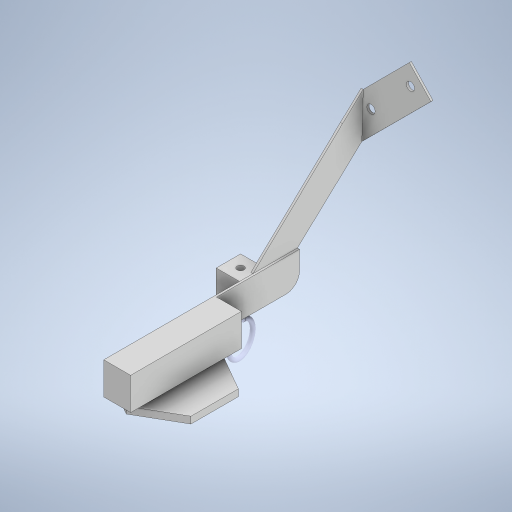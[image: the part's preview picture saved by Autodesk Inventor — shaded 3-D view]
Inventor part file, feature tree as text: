
AUTODESK INVENTOR PART (.ipt)
format: ipt  version: 2023 (Build 270158000, 158)  size: 340,992 bytes
history: native  units: in
note: dims shown in document units (in); Inventor stores cm internally (conversion verified against a paired STEP export)
features: other x5, extrude x1, sketch x1
ambient origin geometry x8: Origin, YZ Plane, XZ Plane, XY Plane, X Axis, Y Axis, Z Axis, Center Point
bodies: Solid1 (feature_tree)
feature tree (7):
  other  "tool.iam"
  other  "Welds"
  other  "ventosas.ipt:1"
  other  "Gancho.ipt:1"
  other  "adaptador.ipt:1"
  extrude  "Extrusion1"  Depth=0.1969in
  sketch  "Sketch1"  dims[d0=0.3937in d1=0.5906in d2=1.378in d4=1.378in d5=1.378in d6=0.1969in d7=0.0in]
